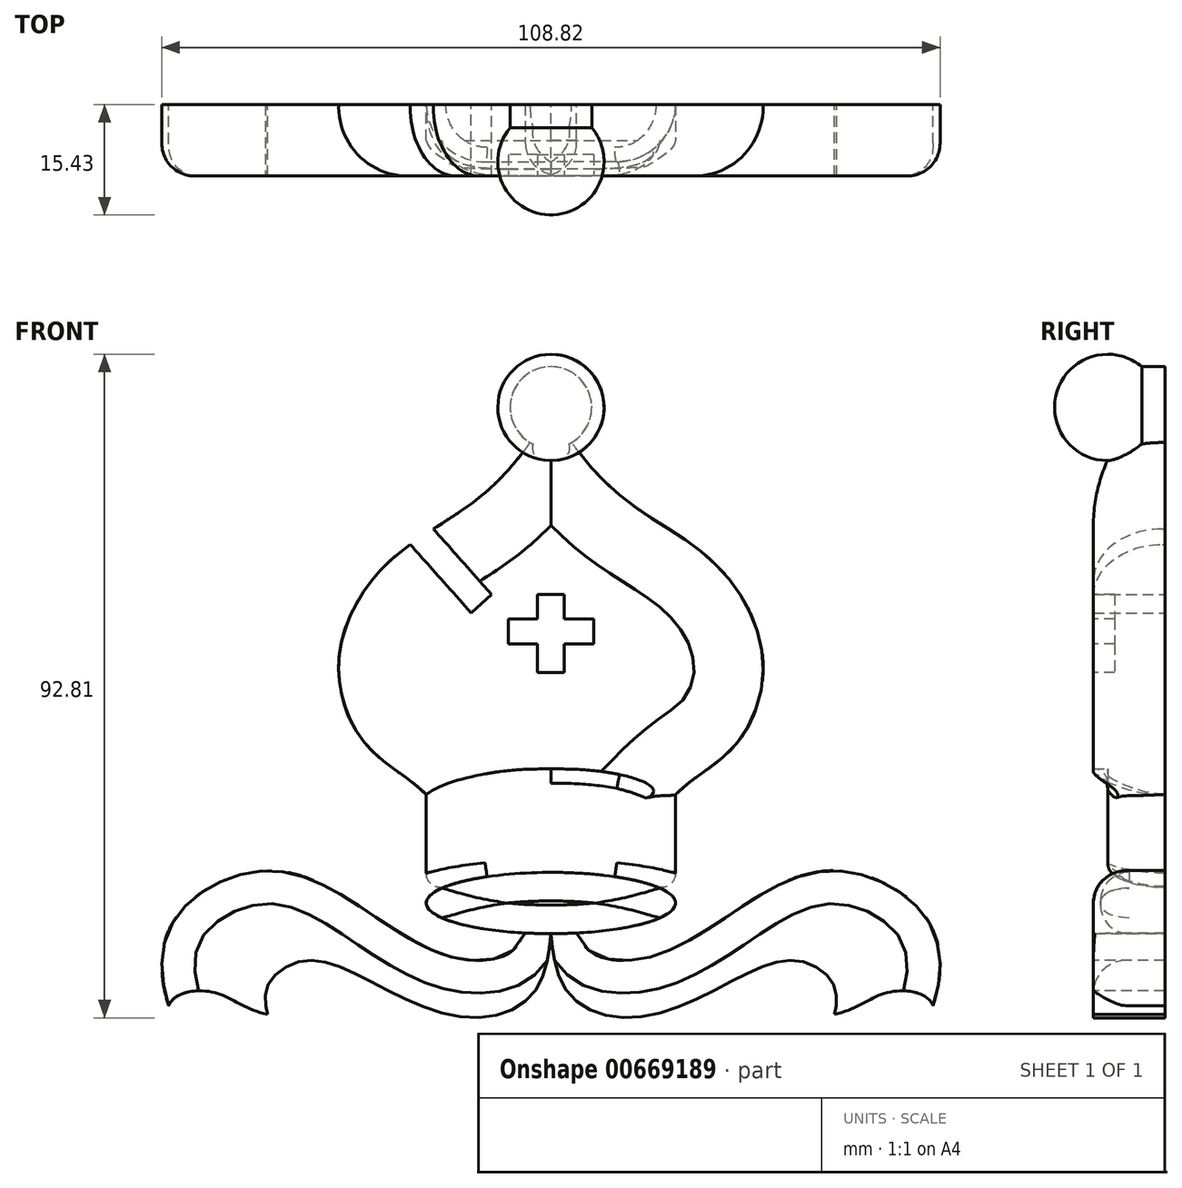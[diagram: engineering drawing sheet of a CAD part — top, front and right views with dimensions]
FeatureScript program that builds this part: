
annotation { "Feature Type Name" : "Feature", "Feature Type Description" : "" }
export const myFeature = defineFeature(function(context is Context, id is Id, definition is map)
    precondition{}
    {
        {
            var Q0;
            Q0=qCreatedBy(makeId("Front.planeOp"),FACE);
            var sketch = newSketch(context, id + "F0", { "sketchPlane" : qUnion([Q0])});
            skEllipticalArc(sketch, "E0", {});
            skLineSegment(sketch, "E1", {"start": v(-17.42, -43.14) * mm, "end": v(-17.42, -27.95) * mm});
            skFitSpline(sketch, "E2", {"points": [v(-17.42, -27.95) * mm, v(-14.5, -26.43) * mm, v(-6.68, -24.7) * mm, v(0, -24.37) * mm], "startDerivative": vector(9.44, 6.74) * mm, "endDerivative": vector(17.65, 0.16) * mm});
            skFitSpline(sketch, "E3", {"points": [v(-17.42, -27.95) * mm, v(-25.91, -20.88) * mm, v(-29.56, -8.3) * mm, v(-22.25, 4.95) * mm, v(-9.13, 14.32) * mm, v(0, 26.18) * mm], "startDerivative": vector(-41.22, 41.68) * mm, "endDerivative": vector(21.3, 47.66) * mm});
            skFitSpline(sketch, "E4", {"points": [v(-3.58, -47.33) * mm, v(-6.03, -50.27) * mm, v(-13.7, -50.73) * mm, v(-25.05, -44.75) * mm, v(-39, -38.62) * mm, v(-52.35, -45.06) * mm, v(-53.43, -57.48) * mm], "startDerivative": vector(-18.13, -34.13) * mm, "endDerivative": vector(24.67, -74.13) * mm});
            skFitSpline(sketch, "E5", {"points": [v(-53.43, -57.48) * mm, v(-47.14, -55.64) * mm, v(-39.62, -58.71) * mm], "startDerivative": vector(4.8, 12.38) * mm, "endDerivative": vector(19.04, -3.92) * mm});
            skFitSpline(sketch, "E6", {"points": [v(-39.62, -58.71) * mm, v(-39.62, -54.72) * mm, v(-34.4, -51.2) * mm, v(-25.5, -53.96) * mm, v(-11.55, -59.17) * mm, v(-2.04, -55.18) * mm, v(0, -47.42) * mm], "startDerivative": vector(-5.97, 26.25) * mm, "endDerivative": vector(3.61, 30.76) * mm});
            skArc(sketch, "E7", {"start": v(0, 31.88) * mm, "mid": v(-5.7, 26.18) * mm, "end": v(0, 20.48) * mm});
            skLineSegment(sketch, "E8", {"start": v(0, 39.92) * mm, "end": v(0, -73.6) * mm, "construction": true});
            skLineSegment(sketch, "E9", {"start": v(0, 31.88) * mm, "end": v(0, -47.42) * mm});
            const initialGuessF0  = {"E0": [0, -0.04313776642084122, 1, 0, 0.017422931268811226, 0.004284881126286053, 1.5707963267948966, 4.71238898038469]};
            skSetInitialGuess(sketch, initialGuessF0);
            skSolve(sketch);
        }
        {
            var Q0;
            {var subQ0=sQuery(id+"F0.wireOp",EDGE,"E2");Q0=makeQuery(id+"F0.imprint","IMPRINT",FACE,{"disambiguationData":[TD([[makeQuery(id+"F0.imprint","IMPRINT",EDGE,{"derivedFrom":subQ0}),1.0]])]});}
            var Q1;
            {var subQ2=sQuery(id+"F0.wireOp",EDGE,"E4");Q1=makeQuery(id+"F0.imprint","IMPRINT",FACE,{"disambiguationData":[TD([[makeQuery(id+"F0.imprint","IMPRINT",EDGE,{"derivedFrom":subQ2}),1.0]])]});}
            extrude(context, id + "F1", {"entities" : qUnion([Q0, Q1]), "depth" : 10 * mm, "offsetDistance" : 25 * mm});
        }
        {
            var Q0;
            {var subQ0=sQuery(id+"F0.wireOp",EDGE,"E9");var subQ1=sQuery(id+"F0.wireOp",EDGE,"E3");var subQ2=makeQuery(id+"F0.imprint","INTERSECT",VERTEX,{"derivedFrom":[subQ1,subQ0]});Q0=makeQuery(id+"F0.imprint","IMPRINT",FACE,{"disambiguationData":[TD([[makeQuery(id+"F0.imprint","IMPRINT",EDGE,{"disambiguationData":[TD([[subQ2,1.0]])],"derivedFrom":subQ1}),1.0]])]});}
            var Q1;
            {var subQ0=sQuery(id+"F0.wireOp",EDGE,"E9");var subQ1=sQuery(id+"F0.wireOp",EDGE,"E3");var subQ2=makeQuery(id+"F0.imprint","INTERSECT",VERTEX,{"derivedFrom":[subQ1,subQ0]});Q1=makeQuery(id+"F0.imprint","IMPRINT",FACE,{"disambiguationData":[TD([[makeQuery(id+"F0.imprint","IMPRINT",EDGE,{"disambiguationData":[TD([[subQ2,1.0]])],"derivedFrom":subQ1}),-1.0]])]});}
            var Q2;
            {var subQ3=sQuery(id+"F0.wireOp",EDGE,"E1");Q2=makeQuery(id+"F0.imprint","IMPRINT",FACE,{"disambiguationData":[TD([[makeQuery(id+"F0.imprint","IMPRINT",EDGE,{"derivedFrom":subQ3}),-1.0]])]});}
            extrude(context, id + "F2", {"entities" : qUnion([Q0, Q1, Q2]), "operationType" : NewBodyOperationType.ADD, "depth" : 8 * mm, "offsetDistance" : 25 * mm});
        }
        {
            var Q0;
            {var subQ0=sQuery(id+"F0.wireOp",EDGE,"E9");var subQ1=sQuery(id+"F0.wireOp",EDGE,"E0");var subQ2=makeQuery(id+"F0.imprint","INTERSECT",VERTEX,{"derivedFrom":[subQ1,subQ0]});Q0=makeQuery(id+"F0.imprint","IMPRINT",FACE,{"disambiguationData":[TD([[makeQuery(id+"F0.imprint","IMPRINT",EDGE,{"disambiguationData":[TD([[subQ2,-1.0]])],"derivedFrom":subQ1}),1.0]])]});}
            extrude(context, id + "F3", {"entities" : qUnion([Q0]), "depth" : 9 * mm, "offsetDistance" : 25 * mm});
        }
        {
            var Q0;
            Q0=makeQuery(id+"F1.opExtrude","SWEPT_BODY",BODY,{"disambiguationData":[OSD([sQuery(id+"F0.wireOp",EDGE,"E2"),sQuery(id+"F0.wireOp",EDGE,"E3"),sQuery(id+"F0.wireOp",EDGE,"E7"),sQuery(id+"F0.wireOp",EDGE,"E9")])]});
            var Q1;
            Q1=makeQuery(id+"F3.opExtrude","SWEPT_BODY",BODY,{"disambiguationData":[OSD([sQuery(id+"F0.wireOp",EDGE,"E0"),sQuery(id+"F0.wireOp",EDGE,"E9")])]});
            var Q2;
            Q2=makeQuery(id+"F1.opExtrude","SWEPT_BODY",BODY,{"disambiguationData":[OSD([sQuery(id+"F0.wireOp",EDGE,"E0"),sQuery(id+"F0.wireOp",EDGE,"E4"),sQuery(id+"F0.wireOp",EDGE,"E5"),sQuery(id+"F0.wireOp",EDGE,"E6")])]});
            var Q3;
            Q3=qCreatedBy(makeId("Right.planeOp"),FACE);
            mirror(context, id + "F4", {"entities" : qUnion([Q0, Q1, Q2]), "mirrorPlane" : qUnion([Q3])});
        }
        {
            var Q0;
            Q0=makeQuery(id+"F2.opExtrude","CAP_FACE",FACE,{"disambiguationData":[OSD([sQuery(id+"F0.wireOp",EDGE,"E7"),sQuery(id+"F0.wireOp",EDGE,"E9")])],"isStart":false});
            var sketch = newSketch(context, id + "F5", { "sketchPlane" : qUnion([Q0])});
            skCircle(sketch, "E10", {"center": v(0, 26.18) * mm, "radius": 7.43 * mm});
            skLineSegment(sketch, "E11", {"start": v(0, 26.18) * mm, "end": v(0, 10.63) * mm});
            skLineSegment(sketch, "E12", {"start": v(0, 10.63) * mm, "end": v(0, 38.12) * mm});
            skSolve(sketch);
        }
        {
            var Q0;
            {var subQ0=sQuery(id+"F0.wireOp",EDGE,"E7");var subQ2=makeQuery(id+"F2.opExtrude","CAP_EDGE",EDGE,{"disambiguationData":[OSD([subQ0])],"isStart":false});var subQ3=makeQuery(id+"F2.boolean.opBoolean","SPLIT",EDGE,{"disambiguationData":[topologyDisambiguationEdgeConnected([makeQuery(id+"F2.opExtrude","SWEPT_FACE",FACE,{"disambiguationData":[OSD([subQ0])]})])],"derivedFrom":subQ2});Q0=makeQuery(id+"F5.imprint","IMPRINT",FACE,{"disambiguationData":[TD([[makeQuery(id+"F5.imprint","IMPRINT",EDGE,{"derivedFrom":subQ3}),-1.0]])]});}
            var Q1;
            {var subQ1=sQuery(id+"F0.wireOp",EDGE,"E7");var subQ3=makeQuery(id+"F2.opExtrude","CAP_EDGE",EDGE,{"disambiguationData":[OSD([subQ1])],"isStart":false});var subQ4=makeQuery(id+"F2.boolean.opBoolean","SPLIT",EDGE,{"disambiguationData":[topologyDisambiguationEdgeConnected([makeQuery(id+"F2.opExtrude","SWEPT_FACE",FACE,{"disambiguationData":[OSD([subQ1])]})])],"derivedFrom":subQ3});Q1=makeQuery(id+"F5.imprint","IMPRINT",FACE,{"disambiguationData":[TD([[makeQuery(id+"F5.imprint","IMPRINT",EDGE,{"derivedFrom":subQ4}),1.0]])]});}
            var Q2;
            Q2=sQuery(id+"F5.wireOp",EDGE,"E12");
            revolve(context, id + "F6", {"entities" : qUnion([Q0, Q1]), "axis" : qUnion([Q2]), "revolveType" : RevolveType.FULL});
        }
        {
            var Q0;
            Q0=makeQuery(id+"F1.opExtrude","CAP_EDGE",EDGE,{"disambiguationData":[OSD([sQuery(id+"F0.wireOp",EDGE,"E3")])],"isStart":false});
            var Q1;
            Q1=makeQuery(id+"F4.opPattern","COPY",EDGE,{"derivedFrom":makeQuery(id+"F1.opExtrude","CAP_EDGE",EDGE,{"disambiguationData":[OSD([sQuery(id+"F0.wireOp",EDGE,"E3")])],"isStart":false}),"instanceName":"1"});
            fillet(context, id + "F7", {"entities" : qUnion([Q0, Q1]), "radius" : 9.66 * mm, "tangentPropagation" : true, "allowEdgeOverflow" : false});
        }
        {
            var Q0;
            Q0=makeQuery(id+"F4.opPattern","COPY",EDGE,{"derivedFrom":makeQuery(id+"F2.opExtrude","CAP_EDGE",EDGE,{"disambiguationData":[OSD([sQuery(id+"F0.wireOp",EDGE,"E1")])],"isStart":false}),"instanceName":"1"});
            var Q1;
            Q1=makeQuery(id+"F2.opExtrude","CAP_EDGE",EDGE,{"disambiguationData":[OSD([sQuery(id+"F0.wireOp",EDGE,"E1")])],"isStart":false});
            fillet(context, id + "F8", {"entities" : qUnion([Q0, Q1]), "radius" : 8.2 * mm, "tangentPropagation" : true, "allowEdgeOverflow" : false});
        }
        {
            var Q0;
            Q0=makeQuery(id+"F2.opExtrude","CAP_EDGE",EDGE,{"disambiguationData":[OSD([sQuery(id+"F0.wireOp",EDGE,"E2")])],"isStart":false});
            var Q1;
            Q1=makeQuery(id+"F4.opPattern","COPY",EDGE,{"derivedFrom":makeQuery(id+"F2.opExtrude","CAP_EDGE",EDGE,{"disambiguationData":[OSD([sQuery(id+"F0.wireOp",EDGE,"E2")])],"isStart":false}),"instanceName":"1"});
            var Q2;
            Q2=makeQuery(id+"F8.opFillet","BLEND_EDGE",EDGE,{"blendedFrom":[makeQuery(id+"F4.opPattern","COPY",EDGE,{"derivedFrom":makeQuery(id+"F2.opExtrude","CAP_EDGE",EDGE,{"disambiguationData":[OSD([sQuery(id+"F0.wireOp",EDGE,"E1")])],"isStart":false}),"instanceName":"1"}),makeQuery(id+"F4.opPattern","COPY",FACE,{"derivedFrom":makeQuery(id+"F1.opExtrude","SWEPT_FACE",FACE,{"disambiguationData":[OSD([sQuery(id+"F0.wireOp",EDGE,"E2")])]}),"instanceName":"1"})],"blendedInto":[makeQuery(id+"F4.opPattern","COPY",FACE,{"derivedFrom":makeQuery(id+"F1.opExtrude","SWEPT_FACE",FACE,{"disambiguationData":[OSD([sQuery(id+"F0.wireOp",EDGE,"E2")])]}),"instanceName":"1"})]});
            fillet(context, id + "F9", {"entities" : qUnion([Q0, Q1, Q2]), "radius" : 2 * mm, "tangentPropagation" : true, "allowEdgeOverflow" : false});
        }
        {
            var Q0;
            Q0=makeQuery(id+"F1.opExtrude","CAP_EDGE",EDGE,{"disambiguationData":[OSD([sQuery(id+"F0.wireOp",EDGE,"E4")])],"isStart":false});
            var Q1;
            Q1=makeQuery(id+"F4.opPattern","COPY",EDGE,{"derivedFrom":makeQuery(id+"F1.opExtrude","CAP_EDGE",EDGE,{"disambiguationData":[OSD([sQuery(id+"F0.wireOp",EDGE,"E4")])],"isStart":false}),"instanceName":"1"});
            fillet(context, id + "F10", {"entities" : qUnion([Q0, Q1]), "radius" : 4.6 * mm, "tangentPropagation" : true, "allowEdgeOverflow" : false});
        }
        {
            var Q0;
            Q0=makeQuery(id+"F3.opExtrude","CAP_EDGE",EDGE,{"disambiguationData":[OSD([sQuery(id+"F0.wireOp",EDGE,"E0")])],"isStart":false});
            var Q1;
            Q1=makeQuery(id+"F4.opPattern","COPY",EDGE,{"derivedFrom":makeQuery(id+"F3.opExtrude","CAP_EDGE",EDGE,{"disambiguationData":[OSD([sQuery(id+"F0.wireOp",EDGE,"E0")])],"isStart":false}),"instanceName":"1"});
            fillet(context, id + "F11", {"entities" : qUnion([Q0, Q1]), "radius" : 4 * mm, "tangentPropagation" : true, "allowEdgeOverflow" : false});
        }
        {
            var Q0;
            Q0=makeQuery(id+"F4.opPattern","COPY",EDGE,{"derivedFrom":makeQuery(id+"F2.opExtrude","CAP_EDGE",EDGE,{"disambiguationData":[OSD([sQuery(id+"F0.wireOp",EDGE,"E0")])],"isStart":false}),"instanceName":"1"});
            var Q1;
            Q1=makeQuery(id+"F2.opExtrude","CAP_EDGE",EDGE,{"disambiguationData":[OSD([sQuery(id+"F0.wireOp",EDGE,"E0")])],"isStart":false});
            fillet(context, id + "F12", {"entities" : qUnion([Q0, Q1]), "radius" : 2 * mm, "tangentPropagation" : true, "allowEdgeOverflow" : false});
        }
        {
            var Q0;
            Q0=makeQuery(id+"F4.opPattern","COPY",BODY,{"derivedFrom":makeQuery(id+"F1.opExtrude","SWEPT_BODY",BODY,{"disambiguationData":[OSD([sQuery(id+"F0.wireOp",EDGE,"E2"),sQuery(id+"F0.wireOp",EDGE,"E3"),sQuery(id+"F0.wireOp",EDGE,"E7"),sQuery(id+"F0.wireOp",EDGE,"E9")])]}),"instanceName":"1"});
            var Q1;
            Q1=makeQuery(id+"F1.opExtrude","SWEPT_BODY",BODY,{"disambiguationData":[OSD([sQuery(id+"F0.wireOp",EDGE,"E0"),sQuery(id+"F0.wireOp",EDGE,"E4"),sQuery(id+"F0.wireOp",EDGE,"E5"),sQuery(id+"F0.wireOp",EDGE,"E6")])]});
            var Q2;
            Q2=makeQuery(id+"F4.opPattern","COPY",BODY,{"derivedFrom":makeQuery(id+"F3.opExtrude","SWEPT_BODY",BODY,{"disambiguationData":[OSD([sQuery(id+"F0.wireOp",EDGE,"E0"),sQuery(id+"F0.wireOp",EDGE,"E9")])]}),"instanceName":"1"});
            var Q3;
            Q3=makeQuery(id+"F6.opRevolve","SWEPT_BODY",BODY,{"disambiguationData":[OSD([sQuery(id+"F5.wireOp",EDGE,"E10"),sQuery(id+"F5.wireOp",EDGE,"E12")])]});
            var Q4;
            Q4=makeQuery(id+"F3.opExtrude","SWEPT_BODY",BODY,{"disambiguationData":[OSD([sQuery(id+"F0.wireOp",EDGE,"E0"),sQuery(id+"F0.wireOp",EDGE,"E9")])]});
            var Q5;
            Q5=makeQuery(id+"F4.opPattern","COPY",BODY,{"derivedFrom":makeQuery(id+"F1.opExtrude","SWEPT_BODY",BODY,{"disambiguationData":[OSD([sQuery(id+"F0.wireOp",EDGE,"E0"),sQuery(id+"F0.wireOp",EDGE,"E4"),sQuery(id+"F0.wireOp",EDGE,"E5"),sQuery(id+"F0.wireOp",EDGE,"E6")])]}),"instanceName":"1"});
            var Q6;
            Q6=makeQuery(id+"F1.opExtrude","SWEPT_BODY",BODY,{"disambiguationData":[OSD([sQuery(id+"F0.wireOp",EDGE,"E2"),sQuery(id+"F0.wireOp",EDGE,"E3"),sQuery(id+"F0.wireOp",EDGE,"E7"),sQuery(id+"F0.wireOp",EDGE,"E9")])]});
            booleanBodies(context, id + "F13", {"operationType" : BooleanOperationType.UNION, "tools" : qUnion([Q0, Q1, Q2, Q3, Q4, Q5, Q6])});
        }
        {
            var Q0;
            {var subQ0=makeQuery(id+"F1.opExtrude","CAP_FACE",FACE,{"disambiguationData":[OSD([sQuery(id+"F0.wireOp",EDGE,"E2"),sQuery(id+"F0.wireOp",EDGE,"E3"),sQuery(id+"F0.wireOp",EDGE,"E7"),sQuery(id+"F0.wireOp",EDGE,"E9")])],"isStart":false});Q0=makeQuery(id+"F13.opBoolean","MERGE",FACE,{"derivedFrom":[subQ0,makeQuery(id+"F4.opPattern","COPY",FACE,{"derivedFrom":subQ0,"instanceName":"1"})]});}
            var sketch = newSketch(context, id + "F14", { "sketchPlane" : qUnion([Q0])});
            skLineSegment(sketch, "E13", {"start": v(-30.59, 19.3) * mm, "end": v(-11.16, -2.56) * mm});
            skLineSegment(sketch, "E14", {"start": v(-11.16, -2.56) * mm, "end": v(-8.27, 0) * mm});
            skLineSegment(sketch, "E15", {"start": v(-8.27, 0) * mm, "end": v(-27.38, 21.5) * mm});
            skLineSegment(sketch, "E16", {"start": v(-27.38, 21.5) * mm, "end": v(-30.59, 19.3) * mm});
            skSolve(sketch);
        }
        {
            var Q0;
            Q0 = qSketchRegion(id + "F14", true);
            extrude(context, id + "F15", {"entities" : qUnion([Q0]), "operationType" : NewBodyOperationType.REMOVE, "endBound" : BoundingType.SYMMETRIC, "depth" : 25 * mm, "offsetDistance" : 25 * mm});
        }
        {
            var Q0;
            {var subQ0=makeQuery(id+"F1.opExtrude","CAP_FACE",FACE,{"disambiguationData":[OSD([sQuery(id+"F0.wireOp",EDGE,"E2"),sQuery(id+"F0.wireOp",EDGE,"E3"),sQuery(id+"F0.wireOp",EDGE,"E7"),sQuery(id+"F0.wireOp",EDGE,"E9")])],"isStart":false});Q0=makeQuery(id+"F13.opBoolean","MERGE",FACE,{"derivedFrom":[subQ0,makeQuery(id+"F4.opPattern","COPY",FACE,{"derivedFrom":subQ0,"instanceName":"1"})]});}
            var sketch = newSketch(context, id + "F16", { "sketchPlane" : qUnion([Q0])});
            skLineSegment(sketch, "E17", {"start": v(0, 0) * mm, "end": v(1.87, 0) * mm});
            skLineSegment(sketch, "E18", {"start": v(1.87, 0) * mm, "end": v(1.87, -3.42) * mm});
            skLineSegment(sketch, "E19", {"start": v(1.87, -3.42) * mm, "end": v(5.97, -3.42) * mm});
            skLineSegment(sketch, "E20", {"start": v(5.97, -3.42) * mm, "end": v(5.97, -6.91) * mm});
            skLineSegment(sketch, "E21", {"start": v(5.97, -6.91) * mm, "end": v(1.87, -6.91) * mm});
            skLineSegment(sketch, "E22", {"start": v(1.87, -6.91) * mm, "end": v(1.87, -10.88) * mm});
            skLineSegment(sketch, "E23", {"start": v(1.87, -10.88) * mm, "end": v(0, -10.88) * mm});
            skLineSegment(sketch, "E24.MirrorCS", {"start": v(0, 0) * mm, "end": v(-1.87, 0) * mm});
            skLineSegment(sketch, "E25.MirrorCS", {"start": v(-1.87, 0) * mm, "end": v(-1.87, -3.42) * mm});
            skLineSegment(sketch, "E26.MirrorCS", {"start": v(-1.87, -3.42) * mm, "end": v(-5.97, -3.42) * mm});
            skLineSegment(sketch, "E27.MirrorCS", {"start": v(-5.97, -3.42) * mm, "end": v(-5.97, -6.91) * mm});
            skLineSegment(sketch, "E28.MirrorCS", {"start": v(-1.87, -6.91) * mm, "end": v(-1.87, -10.88) * mm});
            skLineSegment(sketch, "E29.MirrorCS", {"start": v(-1.87, -10.88) * mm, "end": v(0, -10.88) * mm});
            skLineSegment(sketch, "E30.MirrorCS", {"start": v(-5.97, -6.91) * mm, "end": v(-1.87, -6.91) * mm});
            skSolve(sketch);
        }
        {
            var Q0;
            Q0 = qSketchRegion(id + "F16", true);
            extrude(context, id + "F17", {"entities" : qUnion([Q0]), "operationType" : NewBodyOperationType.REMOVE, "oppositeDirection" : true, "depth" : 3 * mm, "offsetDistance" : 25 * mm});
        }
    });
